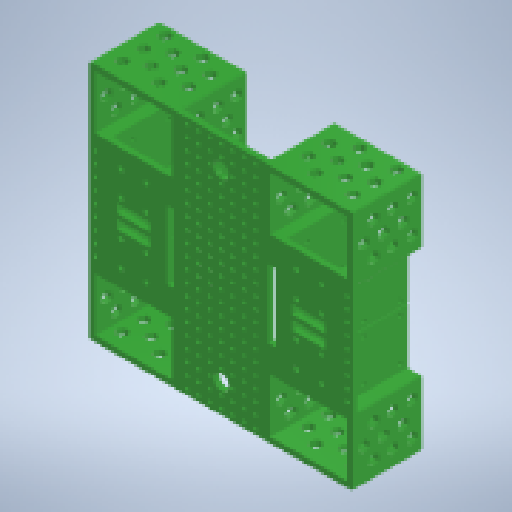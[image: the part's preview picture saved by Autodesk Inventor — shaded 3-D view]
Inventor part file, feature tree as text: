
AUTODESK INVENTOR PART (.ipt)
format: ipt  version: 2024.2 (Build 282272000, 272)  size: 1,504,256 bytes
history: native  units: mm
features: other x27, sketch x11, extrude x10, mirror x6, fillet x2, projected_geometry x1
ambient origin geometry x8: Origin, YZ Plane, XZ Plane, XY Plane, X Axis, Y Axis, Z Axis, Center Point
bodies: Body1 (feature_tree)
feature tree (57):
  extrude  "Extrusion2"  Depth=5.0mm
  sketch  "Esquisse3"
  other  "Plan de construction1"
  extrude  "Extrusion3"  Depth=5.0mm
  other  "Epaississement1"
  other  "Epaississement2"
  extrude  "Extrusion6"  Depth=5.0mm
  fillet  "Congé1"  Radius=5.0mm
  fillet  "Congé2"  Radius=5.0mm
  extrude  "Extrusion8"  Depth=5.0mm
  sketch  "Esquisse9"
  extrude  "Extrusion9"  Depth=5.0mm
  extrude  "Extrusion10"  Depth=5.0mm
  extrude  "Extrusion11"  Depth=3.0mm
  mirror  "Symétrie1"
  mirror  "Symétrie2"
  extrude  "Extrusion12"  Depth=3.0mm
  mirror  "Symétrie3"
  mirror  "Symétrie4"
  extrude  "Extrusion13"  Depth=50.25mm TaperAngle=0.0deg
  mirror  "Symétrie5"
  extrude  "Extrusion14"  Depth=0.15mm
  mirror  "Symétrie6"
  sketch  "Esquisse1"
  other  "Référence1"
  other  "Référence2"
  other  "Référence3"
  other  "Référence4"
  other  "Référence5"
  other  "Référence6"
  other  "Référence7"
  other  "Référence8"
  projected_geometry  "Boucle projetée1"
  sketch  "Esquisse6"
  other  "Référence9"
  other  "Référence10"
  sketch  "Esquisse8"
  other  "Référence15"
  other  "Référence16"
  other  "Référence17"
  other  "Référence18"
  other  "Référence19"
  other  "Référence20"
  sketch  "Esquisse10"
  sketch  "Esquisse11"
  sketch  "Esquisse12"
  other  "Référence21"
  other  "Plan de construction2"
  other  "Plan de construction3"
  other  "Plan de construction4"
  sketch  "Esquisse13"
  sketch  "Esquisse14"
  sketch  "Esquisse15"
  other  "<userpath>\Desktop\Robot\Robotbebou.iam"
  other  "Robotbebou.iam"
  other  "embase_pla:1"
  other  "SF2423-10B41:2"
